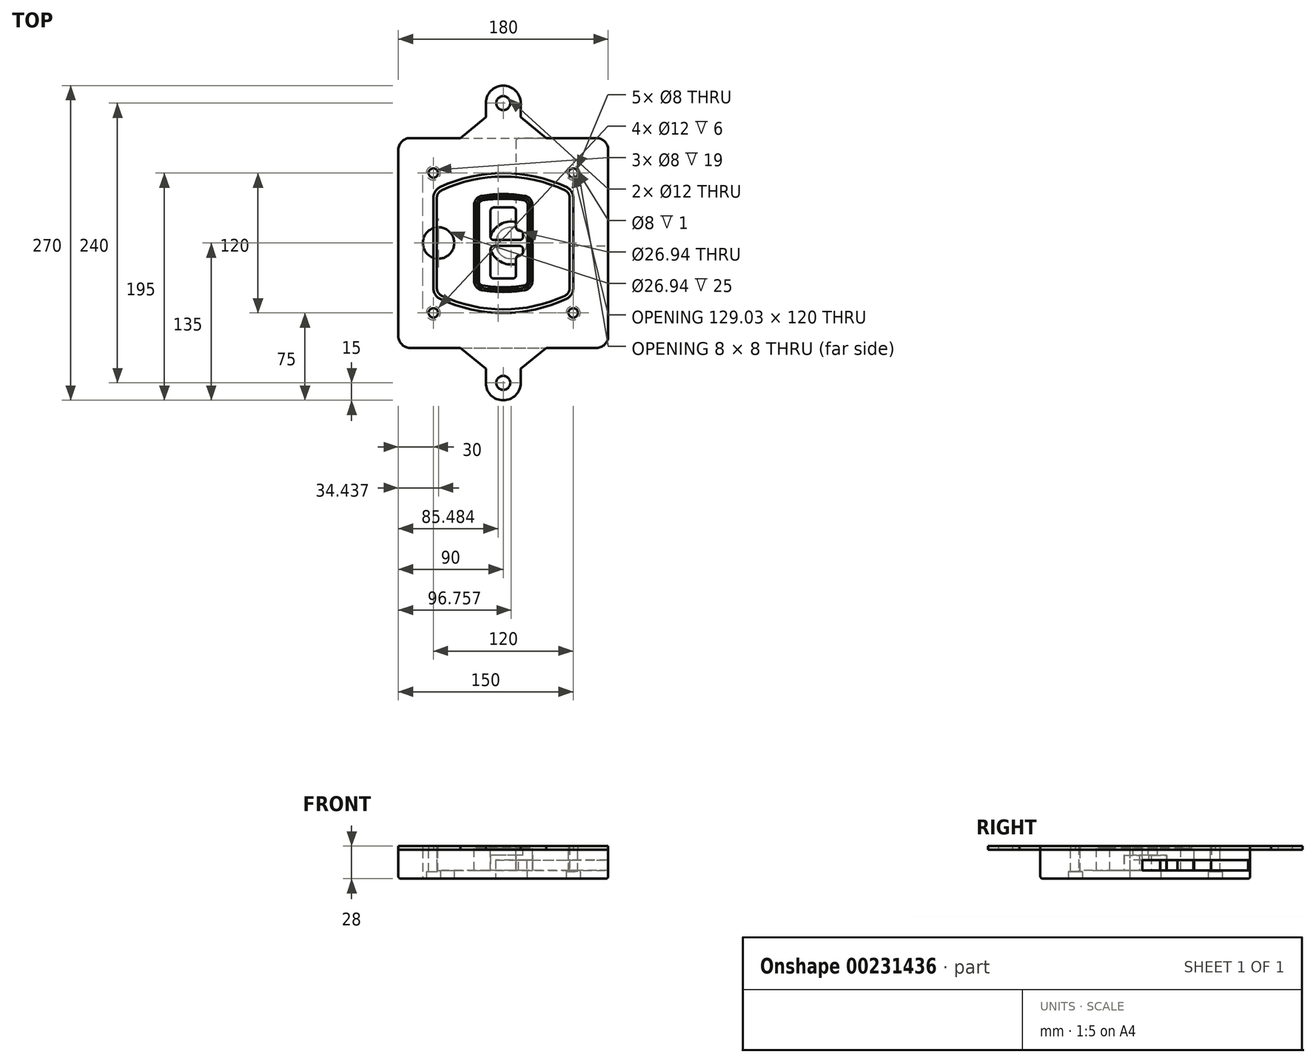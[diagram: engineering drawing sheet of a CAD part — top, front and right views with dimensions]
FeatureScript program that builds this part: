
annotation { "Feature Type Name" : "Feature", "Feature Type Description" : "" }
export const myFeature = defineFeature(function(context is Context, id is Id, definition is map)
    precondition{}
    {
        {
            var Q0;
            Q0=qCreatedBy(makeId("Top.planeOp"),FACE);
            var sketch = newSketch(context, id + "F0", { "sketchPlane" : qUnion([Q0])});
            skPoint(sketch, "E0.rect.middle", {"position": v(0, 0) * mm});
            skLineSegment(sketch, "E1.bottom", {"start": v(-80, -90) * mm, "end": v(80, -90) * mm});
            skLineSegment(sketch, "E1.top", {"start": v(-80, 90) * mm, "end": v(80, 90) * mm});
            skLineSegment(sketch, "E1.left", {"start": v(-90, -80) * mm, "end": v(-90, 80) * mm});
            skLineSegment(sketch, "E1.right", {"start": v(90, -80) * mm, "end": v(90, 80) * mm});
            skLineSegment(sketch, "E2", {"start": v(-90, 90) * mm, "end": v(90, -90) * mm, "construction": true});
            skLineSegment(sketch, "E3", {"start": v(90, 90) * mm, "end": v(-90, -90) * mm, "construction": true});
            skCircle(sketch, "E4", {"center": v(-60, 60) * mm, "radius": 4 * mm});
            skCircle(sketch, "E5", {"center": v(60, 60) * mm, "radius": 4 * mm});
            skCircle(sketch, "E6", {"center": v(60, -60) * mm, "radius": 4 * mm});
            skCircle(sketch, "E7", {"center": v(-60, -60) * mm, "radius": 4 * mm});
            skLineSegment(sketch, "E8", {"start": v(-60, 60) * mm, "end": v(60, 60) * mm, "construction": true});
            skLineSegment(sketch, "E9", {"start": v(60, 60) * mm, "end": v(60, -60) * mm, "construction": true});
            skLineSegment(sketch, "E10", {"start": v(60, -60) * mm, "end": v(-60, -60) * mm, "construction": true});
            skLineSegment(sketch, "E11", {"start": v(-60, -60) * mm, "end": v(-60, 60) * mm, "construction": true});
            skLineSegment(sketch, "E12", {"start": v(-60, 38.83) * mm, "end": v(-60, -38.83) * mm});
            skLineSegment(sketch, "E13", {"start": v(60, 38.83) * mm, "end": v(60, -38.83) * mm});
            skArc(sketch, "E14", {"start": v(54.26, 47.88) * mm, "mid": v(0, 60) * mm, "end": v(-54.26, 47.88) * mm});
            skArc(sketch, "E15", {"start": v(-54.26, -47.88) * mm, "mid": v(0, -60) * mm, "end": v(54.26, -47.88) * mm});
            skLineSegment(sketch, "E16", {"start": v(-60, 0) * mm, "end": v(60, 0) * mm, "construction": true});
            skPoint(sketch, "E17.visualSharp", {"position": v(-60, -45) * mm});
            skArc(sketch, "E17.filletArc", {"start": v(-60, -38.83) * mm, "mid": v(-58.44, -44.2) * mm, "end": v(-54.26, -47.88) * mm});
            skPoint(sketch, "E18.visualSharp", {"position": v(-60, 45) * mm});
            skArc(sketch, "E18.filletArc", {"start": v(-54.26, 47.88) * mm, "mid": v(-58.44, 44.2) * mm, "end": v(-60, 38.83) * mm});
            skPoint(sketch, "E19.visualSharp", {"position": v(60, 45) * mm});
            skArc(sketch, "E19.filletArc", {"start": v(60, 38.83) * mm, "mid": v(58.44, 44.2) * mm, "end": v(54.26, 47.88) * mm});
            skPoint(sketch, "E20.visualSharp", {"position": v(60, -45) * mm});
            skArc(sketch, "E20.filletArc", {"start": v(54.26, -47.88) * mm, "mid": v(58.44, -44.2) * mm, "end": v(60, -38.83) * mm});
            skPoint(sketch, "E21.visualSharp", {"position": v(-90, 90) * mm});
            skArc(sketch, "E21.filletArc", {"start": v(-80, 90) * mm, "mid": v(-87.07, 87.07) * mm, "end": v(-90, 80) * mm});
            skPoint(sketch, "E22.visualSharp", {"position": v(90, 90) * mm});
            skArc(sketch, "E22.filletArc", {"start": v(90, 80) * mm, "mid": v(87.07, 87.07) * mm, "end": v(80, 90) * mm});
            skPoint(sketch, "E23.visualSharp", {"position": v(90, -90) * mm});
            skArc(sketch, "E23.filletArc", {"start": v(80, -90) * mm, "mid": v(87.07, -87.07) * mm, "end": v(90, -80) * mm});
            skPoint(sketch, "E24.visualSharp", {"position": v(-90, -90) * mm});
            skArc(sketch, "E24.filletArc", {"start": v(-90, -80) * mm, "mid": v(-87.07, -87.07) * mm, "end": v(-80, -90) * mm});
            skArc(sketch, "E25.0", {"start": v(57, 38.83) * mm, "mid": v(55.9, 42.58) * mm, "end": v(52.98, 45.17) * mm});
            skLineSegment(sketch, "E25.1", {"start": v(57, 38.83) * mm, "end": v(57, -38.83) * mm});
            skArc(sketch, "E25.2", {"start": v(52.98, -45.17) * mm, "mid": v(55.9, -42.58) * mm, "end": v(57, -38.83) * mm});
            skArc(sketch, "E25.3", {"start": v(-52.98, -45.17) * mm, "mid": v(0, -57) * mm, "end": v(52.98, -45.17) * mm});
            skArc(sketch, "E25.4", {"start": v(-57, -38.83) * mm, "mid": v(-55.9, -42.58) * mm, "end": v(-52.98, -45.17) * mm});
            skArc(sketch, "E25.5", {"start": v(52.98, 45.17) * mm, "mid": v(0, 57) * mm, "end": v(-52.98, 45.17) * mm});
            skLineSegment(sketch, "E25.6", {"start": v(-57, 38.83) * mm, "end": v(-57, -38.83) * mm});
            skArc(sketch, "E25.7", {"start": v(-52.98, 45.17) * mm, "mid": v(-55.9, 42.58) * mm, "end": v(-57, 38.83) * mm});
            skArc(sketch, "E26.0", {"start": v(-55.96, 51.5) * mm, "mid": v(-61.82, 46.33) * mm, "end": v(-64, 38.83) * mm});
            skArc(sketch, "E26.1", {"start": v(55.96, 51.5) * mm, "mid": v(0, 64) * mm, "end": v(-55.96, 51.5) * mm});
            skArc(sketch, "E26.2", {"start": v(64, 38.83) * mm, "mid": v(61.82, 46.33) * mm, "end": v(55.96, 51.5) * mm});
            skLineSegment(sketch, "E26.3", {"start": v(64, 38.83) * mm, "end": v(64, -38.83) * mm});
            skArc(sketch, "E26.4", {"start": v(55.96, -51.5) * mm, "mid": v(61.82, -46.33) * mm, "end": v(64, -38.83) * mm});
            skLineSegment(sketch, "E26.5", {"start": v(-64, 38.83) * mm, "end": v(-64, -38.83) * mm});
            skArc(sketch, "E26.6", {"start": v(-55.96, -51.5) * mm, "mid": v(0, -64) * mm, "end": v(55.96, -51.5) * mm});
            skArc(sketch, "E26.7", {"start": v(-64, -38.83) * mm, "mid": v(-61.82, -46.33) * mm, "end": v(-55.96, -51.5) * mm});
            skSolve(sketch);
        }
        {
            var Q0;
            Q0=makeQuery(id+"F0.imprint","IMPRINT",FACE,{"disambiguationData":[TD([[makeQuery(id+"F0.imprint","IMPRINT",EDGE,{"derivedFrom":sQuery(id+"F0.wireOp",EDGE,"E1.bottom")}),1.0]])]});
            var Q1;
            Q1=makeQuery(id+"F0.imprint","IMPRINT",FACE,{"disambiguationData":[TD([[makeQuery(id+"F0.imprint","IMPRINT",EDGE,{"derivedFrom":sQuery(id+"F0.wireOp",EDGE,"E12")}),1.0]])]});
            var Q2;
            Q2=makeQuery(id+"F0.imprint","IMPRINT",FACE,{"disambiguationData":[TD([[makeQuery(id+"F0.imprint","IMPRINT",EDGE,{"derivedFrom":sQuery(id+"F0.wireOp",EDGE,"E25.0")}),1.0]])]});
            var Q3;
            Q3=makeQuery(id+"F0.imprint","IMPRINT",FACE,{"disambiguationData":[TD([[makeQuery(id+"F0.imprint","IMPRINT",EDGE,{"derivedFrom":sQuery(id+"F0.wireOp",EDGE,"E12")}),-1.0]])]});
            extrude(context, id + "F1", {"entities" : qUnion([Q0, Q1, Q2, Q3]), "oppositeDirection" : true, "depth" : 25 * mm});
        }
        {
            var Q0;
            Q0=makeQuery(id+"F0.imprint","IMPRINT",FACE,{"disambiguationData":[TD([[makeQuery(id+"F0.imprint","IMPRINT",EDGE,{"derivedFrom":sQuery(id+"F0.wireOp",EDGE,"E12")}),1.0]])]});
            extrude(context, id + "F2", {"entities" : qUnion([Q0]), "operationType" : NewBodyOperationType.ADD, "depth" : 3 * mm});
        }
        {
            var Q0;
            Q0=makeQuery(id+"F0.imprint","IMPRINT",FACE,{"disambiguationData":[TD([[makeQuery(id+"F0.imprint","IMPRINT",EDGE,{"derivedFrom":sQuery(id+"F0.wireOp",EDGE,"E25.0")}),1.0]])]});
            extrude(context, id + "F3", {"entities" : qUnion([Q0]), "operationType" : NewBodyOperationType.REMOVE, "oppositeDirection" : true, "depth" : 18 * mm});
        }
        {
            var Q0;
            Q0=makeQuery(id+"F2.opExtrude","CAP_FACE",FACE,{"disambiguationData":[OSD([sQuery(id+"F0.wireOp",EDGE,"E12"),sQuery(id+"F0.wireOp",EDGE,"E13"),sQuery(id+"F0.wireOp",EDGE,"E14"),sQuery(id+"F0.wireOp",EDGE,"E15"),sQuery(id+"F0.wireOp",EDGE,"E17.filletArc"),sQuery(id+"F0.wireOp",EDGE,"E18.filletArc"),sQuery(id+"F0.wireOp",EDGE,"E19.filletArc"),sQuery(id+"F0.wireOp",EDGE,"E20.filletArc"),sQuery(id+"F0.wireOp",EDGE,"E25.0"),sQuery(id+"F0.wireOp",EDGE,"E25.1"),sQuery(id+"F0.wireOp",EDGE,"E25.2"),sQuery(id+"F0.wireOp",EDGE,"E25.3"),sQuery(id+"F0.wireOp",EDGE,"E25.4"),sQuery(id+"F0.wireOp",EDGE,"E25.5"),sQuery(id+"F0.wireOp",EDGE,"E25.6"),sQuery(id+"F0.wireOp",EDGE,"E25.7")])],"isStart":false});
            var sketch = newSketch(context, id + "F4", { "sketchPlane" : qUnion([Q0])});
            skArc(sketch, "E27.0", {"start": v(-18.34, -40.45) * mm, "mid": v(0, -42) * mm, "end": v(18.34, -40.45) * mm});
            skArc(sketch, "E28.0", {"start": v(18.34, 40.45) * mm, "mid": v(0, 42) * mm, "end": v(-18.34, 40.45) * mm});
            skLineSegment(sketch, "E29", {"start": v(-25, 32.57) * mm, "end": v(-25, -32.57) * mm});
            skLineSegment(sketch, "E30", {"start": v(25, 32.57) * mm, "end": v(25, -32.57) * mm});
            skLineSegment(sketch, "E31", {"start": v(-25, 39.1) * mm, "end": v(25, 39.1) * mm, "construction": true});
            skLineSegment(sketch, "E32", {"start": v(-25, -39.1) * mm, "end": v(25, -39.1) * mm, "construction": true});
            skPoint(sketch, "E33.visualSharp", {"position": v(-25, 39.1) * mm});
            skArc(sketch, "E33.filletArc", {"start": v(-18.34, 40.45) * mm, "mid": v(-23.11, 37.73) * mm, "end": v(-25, 32.57) * mm});
            skPoint(sketch, "E34.visualSharp", {"position": v(25, 39.1) * mm});
            skArc(sketch, "E34.filletArc", {"start": v(25, 32.57) * mm, "mid": v(23.11, 37.73) * mm, "end": v(18.34, 40.45) * mm});
            skPoint(sketch, "E35.visualSharp", {"position": v(25, -39.1) * mm});
            skArc(sketch, "E35.filletArc", {"start": v(18.34, -40.45) * mm, "mid": v(23.11, -37.73) * mm, "end": v(25, -32.57) * mm});
            skPoint(sketch, "E36.visualSharp", {"position": v(-25, -39.1) * mm});
            skArc(sketch, "E36.filletArc", {"start": v(-25, -32.57) * mm, "mid": v(-23.11, -37.73) * mm, "end": v(-18.34, -40.45) * mm});
            skArc(sketch, "E37.0", {"start": v(52.98, 45.17) * mm, "mid": v(0, 57) * mm, "end": v(-52.98, 45.17) * mm});
            skArc(sketch, "E37.1", {"start": v(-52.98, 45.17) * mm, "mid": v(-55.9, 42.58) * mm, "end": v(-57, 38.83) * mm});
            skLineSegment(sketch, "E37.2", {"start": v(-57, 38.83) * mm, "end": v(-57, -38.83) * mm});
            skArc(sketch, "E37.3", {"start": v(-57, -38.83) * mm, "mid": v(-55.9, -42.58) * mm, "end": v(-52.98, -45.17) * mm});
            skArc(sketch, "E37.4", {"start": v(-52.98, -45.17) * mm, "mid": v(0, -57) * mm, "end": v(52.98, -45.17) * mm});
            skArc(sketch, "E37.5", {"start": v(52.98, -45.17) * mm, "mid": v(55.9, -42.58) * mm, "end": v(57, -38.83) * mm});
            skLineSegment(sketch, "E37.6", {"start": v(57, 38.83) * mm, "end": v(57, -38.83) * mm});
            skArc(sketch, "E37.7", {"start": v(57, 38.83) * mm, "mid": v(55.9, 42.58) * mm, "end": v(52.98, 45.17) * mm});
            skLineSegment(sketch, "E38.0", {"start": v(23, 32.57) * mm, "end": v(23, -32.57) * mm});
            skArc(sketch, "E38.1", {"start": v(18, -38.48) * mm, "mid": v(21.58, -36.44) * mm, "end": v(23, -32.57) * mm});
            skArc(sketch, "E38.2", {"start": v(-18, -38.48) * mm, "mid": v(0, -40) * mm, "end": v(18, -38.48) * mm});
            skArc(sketch, "E38.3", {"start": v(-23, -32.57) * mm, "mid": v(-21.58, -36.44) * mm, "end": v(-18, -38.48) * mm});
            skLineSegment(sketch, "E38.4", {"start": v(-23, 32.57) * mm, "end": v(-23, -32.57) * mm});
            skArc(sketch, "E38.5", {"start": v(23, 32.57) * mm, "mid": v(21.58, 36.44) * mm, "end": v(18, 38.48) * mm});
            skArc(sketch, "E38.6", {"start": v(-18, 38.48) * mm, "mid": v(-21.58, 36.44) * mm, "end": v(-23, 32.57) * mm});
            skArc(sketch, "E38.7", {"start": v(18, 38.48) * mm, "mid": v(0, 40) * mm, "end": v(-18, 38.48) * mm});
            skArc(sketch, "E39.0", {"start": v(21, 32.57) * mm, "mid": v(20.06, 35.15) * mm, "end": v(17.67, 36.5) * mm});
            skLineSegment(sketch, "E39.1", {"start": v(21, 32.57) * mm, "end": v(21, -32.57) * mm});
            skArc(sketch, "E39.2", {"start": v(17.67, -36.5) * mm, "mid": v(20.06, -35.15) * mm, "end": v(21, -32.57) * mm});
            skArc(sketch, "E39.3", {"start": v(-17.67, -36.5) * mm, "mid": v(0, -38) * mm, "end": v(17.67, -36.5) * mm});
            skArc(sketch, "E39.4", {"start": v(-21, -32.57) * mm, "mid": v(-20.06, -35.15) * mm, "end": v(-17.67, -36.5) * mm});
            skArc(sketch, "E39.5", {"start": v(17.67, 36.5) * mm, "mid": v(0, 38) * mm, "end": v(-17.67, 36.5) * mm});
            skLineSegment(sketch, "E39.6", {"start": v(-21, 32.57) * mm, "end": v(-21, -32.57) * mm});
            skArc(sketch, "E39.7", {"start": v(-17.67, 36.5) * mm, "mid": v(-20.06, 35.15) * mm, "end": v(-21, 32.57) * mm});
            skLineSegment(sketch, "E40", {"start": v(-25, 0) * mm, "end": v(25, 0) * mm, "construction": true});
            skLineSegment(sketch, "E41", {"start": v(-11, 5.5) * mm, "end": v(-11, 27.5) * mm});
            skLineSegment(sketch, "E42", {"start": v(-8, 30.5) * mm, "end": v(8, 30.5) * mm});
            skLineSegment(sketch, "E43", {"start": v(11, 27.5) * mm, "end": v(11, 13.5) * mm});
            skLineSegment(sketch, "E44", {"start": v(14, 10.5) * mm, "end": v(14, 10.5) * mm});
            skLineSegment(sketch, "E45", {"start": v(17, 7.5) * mm, "end": v(17, 5.5) * mm});
            skLineSegment(sketch, "E46", {"start": v(14, 2.5) * mm, "end": v(-8, 2.5) * mm});
            skPoint(sketch, "E47.visualSharp", {"position": v(-11, 30.5) * mm});
            skArc(sketch, "E47.filletArc", {"start": v(-8, 30.5) * mm, "mid": v(-10.12, 29.62) * mm, "end": v(-11, 27.5) * mm});
            skPoint(sketch, "E48.visualSharp", {"position": v(11, 30.5) * mm});
            skArc(sketch, "E48.filletArc", {"start": v(11, 27.5) * mm, "mid": v(10.12, 29.62) * mm, "end": v(8, 30.5) * mm});
            skPoint(sketch, "E49.visualSharp", {"position": v(11, 10.5) * mm});
            skArc(sketch, "E49.filletArc", {"start": v(11, 13.5) * mm, "mid": v(11.88, 11.38) * mm, "end": v(14, 10.5) * mm});
            skPoint(sketch, "E50.visualSharp", {"position": v(17, 10.5) * mm});
            skArc(sketch, "E50.filletArc", {"start": v(17, 7.5) * mm, "mid": v(16.12, 9.62) * mm, "end": v(14, 10.5) * mm});
            skPoint(sketch, "E51.visualSharp", {"position": v(17, 2.5) * mm});
            skArc(sketch, "E51.filletArc", {"start": v(14, 2.5) * mm, "mid": v(16.12, 3.38) * mm, "end": v(17, 5.5) * mm});
            skPoint(sketch, "E52.visualSharp", {"position": v(-11, 2.5) * mm});
            skArc(sketch, "E52.filletArc", {"start": v(-11, 5.5) * mm, "mid": v(-10.12, 3.38) * mm, "end": v(-8, 2.5) * mm});
            skLineSegment(sketch, "E53.0.MirrorCS", {"start": v(14, -2.5) * mm, "end": v(-8, -2.5) * mm});
            skArc(sketch, "E54.0.MirrorCS", {"start": v(-11, -5.5) * mm, "mid": v(-10.12, -3.38) * mm, "end": v(-8, -2.5) * mm});
            skLineSegment(sketch, "E55.0.MirrorCS", {"start": v(-11, -5.5) * mm, "end": v(-11, -27.5) * mm});
            skArc(sketch, "E56.0.MirrorCS", {"start": v(-8, -30.5) * mm, "mid": v(-10.12, -29.62) * mm, "end": v(-11, -27.5) * mm});
            skLineSegment(sketch, "E57.0.MirrorCS", {"start": v(-8, -30.5) * mm, "end": v(8, -30.5) * mm});
            skArc(sketch, "E58.0.MirrorCS", {"start": v(11, -27.5) * mm, "mid": v(10.12, -29.62) * mm, "end": v(8, -30.5) * mm});
            skLineSegment(sketch, "E59.0.MirrorCS", {"start": v(11, -27.5) * mm, "end": v(11, -13.5) * mm});
            skArc(sketch, "E60.0.MirrorCS", {"start": v(11, -13.5) * mm, "mid": v(11.88, -11.38) * mm, "end": v(14, -10.5) * mm});
            skArc(sketch, "E61.0.MirrorCS", {"start": v(17, -7.5) * mm, "mid": v(16.12, -9.62) * mm, "end": v(14, -10.5) * mm});
            skLineSegment(sketch, "E62.0.MirrorCS", {"start": v(17, -7.5) * mm, "end": v(17, -5.5) * mm});
            skArc(sketch, "E63.0.MirrorCS", {"start": v(14, -2.5) * mm, "mid": v(16.12, -3.38) * mm, "end": v(17, -5.5) * mm});
            skSolve(sketch);
        }
        {
            var Q0;
            Q0=makeQuery(id+"F4.imprint","IMPRINT",FACE,{"disambiguationData":[TD([[makeQuery(id+"F4.imprint","IMPRINT",EDGE,{"derivedFrom":sQuery(id+"F4.wireOp",EDGE,"E27.0")}),1.0]])]});
            var Q1;
            Q1=makeQuery(id+"F4.imprint","IMPRINT",FACE,{"disambiguationData":[TD([[makeQuery(id+"F4.imprint","IMPRINT",EDGE,{"derivedFrom":sQuery(id+"F4.wireOp",EDGE,"E38.0")}),-1.0]])]});
            var Q2;
            Q2=makeQuery(id+"F4.imprint","IMPRINT",FACE,{"disambiguationData":[TD([[makeQuery(id+"F4.imprint","IMPRINT",EDGE,{"derivedFrom":sQuery(id+"F4.wireOp",EDGE,"E39.0")}),1.0]])]});
            extrude(context, id + "F5", {"entities" : qUnion([Q0, Q1, Q2]), "operationType" : NewBodyOperationType.ADD, "endBound" : BoundingType.UP_TO_NEXT, "oppositeDirection" : true, "depth" : 25 * mm});
        }
        {
            var Q0;
            Q0=makeQuery(id+"F4.imprint","IMPRINT",FACE,{"disambiguationData":[TD([[makeQuery(id+"F4.imprint","IMPRINT",EDGE,{"derivedFrom":sQuery(id+"F4.wireOp",EDGE,"E38.0")}),-1.0]])]});
            extrude(context, id + "F6", {"entities" : qUnion([Q0]), "operationType" : NewBodyOperationType.REMOVE, "oppositeDirection" : true, "depth" : 2 * mm});
        }
        {
            var Q0;
            Q0=makeQuery(id+"F1.opExtrude","CAP_FACE",FACE,{"disambiguationData":[OSD([sQuery(id+"F0.wireOp",EDGE,"E1.bottom"),sQuery(id+"F0.wireOp",EDGE,"E1.top"),sQuery(id+"F0.wireOp",EDGE,"E1.left"),sQuery(id+"F0.wireOp",EDGE,"E1.right"),sQuery(id+"F0.wireOp",EDGE,"E4"),sQuery(id+"F0.wireOp",EDGE,"E5"),sQuery(id+"F0.wireOp",EDGE,"E6"),sQuery(id+"F0.wireOp",EDGE,"E7"),sQuery(id+"F0.wireOp",EDGE,"E21.filletArc"),sQuery(id+"F0.wireOp",EDGE,"E22.filletArc"),sQuery(id+"F0.wireOp",EDGE,"E23.filletArc"),sQuery(id+"F0.wireOp",EDGE,"E24.filletArc")])],"isStart":false});
            var sketch = newSketch(context, id + "F7", { "sketchPlane" : qUnion([Q0])});
            skCircle(sketch, "E64", {"center": v(6.76, 0) * mm, "radius": 13.47 * mm});
            skCircle(sketch, "E65", {"center": v(-55.56, 0) * mm, "radius": 13.47 * mm});
            skLineSegment(sketch, "E66", {"start": v(90, 0) * mm, "end": v(-90, 0) * mm});
            skCircle(sketch, "E67", {"center": v(6.76, 0) * mm, "radius": 18.47 * mm});
            skCircle(sketch, "E68", {"center": v(60, -60) * mm, "radius": 6 * mm});
            skCircle(sketch, "E69", {"center": v(-60, -60) * mm, "radius": 6 * mm});
            skCircle(sketch, "E70", {"center": v(-60, 60) * mm, "radius": 6 * mm});
            skCircle(sketch, "E71", {"center": v(60, 60) * mm, "radius": 6 * mm});
            skSolve(sketch);
        }
        {
            var Q0;
            {var subQ1=sQuery(id+"F7.wireOp",EDGE,"E66");var subQ4=sQuery(id+"F7.wireOp",EDGE,"E64");var subQ6=makeQuery(id+"F7.imprint","INTERSECT",VERTEX,{"disambiguationData":[OD(0.0)],"derivedFrom":[subQ4,subQ1]});Q0=makeQuery(id+"F7.imprint","IMPRINT",FACE,{"disambiguationData":[TD([[makeQuery(id+"F7.imprint","IMPRINT",EDGE,{"disambiguationData":[TD([[subQ6,-1.0]])],"derivedFrom":subQ4}),-1.0]])]});}
            var Q1;
            {var subQ0=sQuery(id+"F7.wireOp",EDGE,"E66");var subQ1=sQuery(id+"F7.wireOp",EDGE,"E64");var subQ3=makeQuery(id+"F7.imprint","INTERSECT",VERTEX,{"disambiguationData":[OD(0.0)],"derivedFrom":[subQ1,subQ0]});Q1=makeQuery(id+"F7.imprint","IMPRINT",FACE,{"disambiguationData":[TD([[makeQuery(id+"F7.imprint","IMPRINT",EDGE,{"disambiguationData":[TD([[subQ3,-1.0]])],"derivedFrom":subQ1}),1.0]])]});}
            var Q2;
            {var subQ0=sQuery(id+"F7.wireOp",EDGE,"E66");var subQ1=sQuery(id+"F7.wireOp",EDGE,"E64");var subQ3=makeQuery(id+"F7.imprint","INTERSECT",VERTEX,{"disambiguationData":[OD(0.0)],"derivedFrom":[subQ1,subQ0]});Q2=makeQuery(id+"F7.imprint","IMPRINT",FACE,{"disambiguationData":[TD([[makeQuery(id+"F7.imprint","IMPRINT",EDGE,{"disambiguationData":[TD([[subQ3,1.0]])],"derivedFrom":subQ1}),1.0]])]});}
            var Q3;
            {var subQ1=sQuery(id+"F7.wireOp",EDGE,"E66");var subQ4=sQuery(id+"F7.wireOp",EDGE,"E64");var subQ6=makeQuery(id+"F7.imprint","INTERSECT",VERTEX,{"disambiguationData":[OD(0.0)],"derivedFrom":[subQ4,subQ1]});Q3=makeQuery(id+"F7.imprint","IMPRINT",FACE,{"disambiguationData":[TD([[makeQuery(id+"F7.imprint","IMPRINT",EDGE,{"disambiguationData":[TD([[subQ6,1.0]])],"derivedFrom":subQ4}),-1.0]])]});}
            extrude(context, id + "F8", {"entities" : qUnion([Q0, Q1, Q2, Q3]), "operationType" : NewBodyOperationType.ADD, "oppositeDirection" : true, "depth" : 20 * mm});
        }
        {
            var Q0;
            {var subQ0=sQuery(id+"F7.wireOp",EDGE,"E66");var subQ1=sQuery(id+"F7.wireOp",EDGE,"E64");var subQ3=makeQuery(id+"F7.imprint","INTERSECT",VERTEX,{"disambiguationData":[OD(0.0)],"derivedFrom":[subQ1,subQ0]});Q0=makeQuery(id+"F7.imprint","IMPRINT",FACE,{"disambiguationData":[TD([[makeQuery(id+"F7.imprint","IMPRINT",EDGE,{"disambiguationData":[TD([[subQ3,-1.0]])],"derivedFrom":subQ1}),1.0]])]});}
            var Q1;
            {var subQ0=sQuery(id+"F7.wireOp",EDGE,"E66");var subQ1=sQuery(id+"F7.wireOp",EDGE,"E64");var subQ3=makeQuery(id+"F7.imprint","INTERSECT",VERTEX,{"disambiguationData":[OD(0.0)],"derivedFrom":[subQ1,subQ0]});Q1=makeQuery(id+"F7.imprint","IMPRINT",FACE,{"disambiguationData":[TD([[makeQuery(id+"F7.imprint","IMPRINT",EDGE,{"disambiguationData":[TD([[subQ3,1.0]])],"derivedFrom":subQ1}),1.0]])]});}
            extrude(context, id + "F9", {"entities" : qUnion([Q0, Q1]), "operationType" : NewBodyOperationType.REMOVE, "oppositeDirection" : true, "depth" : 16 * mm});
        }
        {
            var Q0;
            {var subQ0=sQuery(id+"F7.wireOp",EDGE,"E66");var subQ1=sQuery(id+"F7.wireOp",EDGE,"E65");var subQ3=makeQuery(id+"F7.imprint","INTERSECT",VERTEX,{"disambiguationData":[OD(0.0)],"derivedFrom":[subQ1,subQ0]});Q0=makeQuery(id+"F7.imprint","IMPRINT",FACE,{"disambiguationData":[TD([[makeQuery(id+"F7.imprint","IMPRINT",EDGE,{"disambiguationData":[TD([[subQ3,-1.0]])],"derivedFrom":subQ1}),1.0]])]});}
            var Q1;
            {var subQ0=sQuery(id+"F7.wireOp",EDGE,"E66");var subQ1=sQuery(id+"F7.wireOp",EDGE,"E65");var subQ3=makeQuery(id+"F7.imprint","INTERSECT",VERTEX,{"disambiguationData":[OD(0.0)],"derivedFrom":[subQ1,subQ0]});Q1=makeQuery(id+"F7.imprint","IMPRINT",FACE,{"disambiguationData":[TD([[makeQuery(id+"F7.imprint","IMPRINT",EDGE,{"disambiguationData":[TD([[subQ3,1.0]])],"derivedFrom":subQ1}),1.0]])]});}
            extrude(context, id + "F10", {"entities" : qUnion([Q0, Q1]), "operationType" : NewBodyOperationType.REMOVE, "oppositeDirection" : true, "depth" : 25 * mm});
        }
        {
            var Q0;
            Q0=makeQuery(id+"F7.imprint","IMPRINT",FACE,{"disambiguationData":[TD([[makeQuery(id+"F7.imprint","IMPRINT",EDGE,{"derivedFrom":sQuery(id+"F7.wireOp",EDGE,"E68")}),1.0]])]});
            var Q1;
            Q1=makeQuery(id+"F7.imprint","IMPRINT",FACE,{"disambiguationData":[TD([[makeQuery(id+"F7.imprint","IMPRINT",EDGE,{"derivedFrom":makeQuery(id+"F1.opExtrude","CAP_EDGE",EDGE,{"disambiguationData":[OSD([sQuery(id+"F0.wireOp",EDGE,"E5")])],"isStart":false})}),-1.0]])]});
            var Q2;
            Q2=makeQuery(id+"F7.imprint","IMPRINT",FACE,{"disambiguationData":[TD([[makeQuery(id+"F7.imprint","IMPRINT",EDGE,{"derivedFrom":sQuery(id+"F7.wireOp",EDGE,"E69")}),1.0]])]});
            var Q3;
            Q3=makeQuery(id+"F7.imprint","IMPRINT",FACE,{"disambiguationData":[TD([[makeQuery(id+"F7.imprint","IMPRINT",EDGE,{"derivedFrom":makeQuery(id+"F1.opExtrude","CAP_EDGE",EDGE,{"disambiguationData":[OSD([sQuery(id+"F0.wireOp",EDGE,"E4")])],"isStart":false})}),-1.0]])]});
            var Q4;
            Q4=makeQuery(id+"F7.imprint","IMPRINT",FACE,{"disambiguationData":[TD([[makeQuery(id+"F7.imprint","IMPRINT",EDGE,{"derivedFrom":sQuery(id+"F7.wireOp",EDGE,"E70")}),1.0]])]});
            var Q5;
            Q5=makeQuery(id+"F7.imprint","IMPRINT",FACE,{"disambiguationData":[TD([[makeQuery(id+"F7.imprint","IMPRINT",EDGE,{"derivedFrom":makeQuery(id+"F1.opExtrude","CAP_EDGE",EDGE,{"disambiguationData":[OSD([sQuery(id+"F0.wireOp",EDGE,"E7")])],"isStart":false})}),-1.0]])]});
            var Q6;
            Q6=makeQuery(id+"F7.imprint","IMPRINT",FACE,{"disambiguationData":[TD([[makeQuery(id+"F7.imprint","IMPRINT",EDGE,{"derivedFrom":sQuery(id+"F7.wireOp",EDGE,"E71")}),1.0]])]});
            var Q7;
            Q7=makeQuery(id+"F7.imprint","IMPRINT",FACE,{"disambiguationData":[TD([[makeQuery(id+"F7.imprint","IMPRINT",EDGE,{"derivedFrom":makeQuery(id+"F1.opExtrude","CAP_EDGE",EDGE,{"disambiguationData":[OSD([sQuery(id+"F0.wireOp",EDGE,"E6")])],"isStart":false})}),-1.0]])]});
            extrude(context, id + "F11", {"entities" : qUnion([Q0, Q1, Q2, Q3, Q4, Q5, Q6, Q7]), "operationType" : NewBodyOperationType.REMOVE, "oppositeDirection" : true, "depth" : 6 * mm});
        }
        {
            var Q0;
            Q0=makeQuery(id+"F9.boolean.opBoolean","COPY",FACE,{"derivedFrom":makeQuery(id+"F9.opExtrude","CAP_FACE",FACE,{"disambiguationData":[OSD([sQuery(id+"F7.wireOp",EDGE,"E64")])],"isStart":false})});
            var sketch = newSketch(context, id + "F12", { "sketchPlane" : qUnion([Q0])});
            skArc(sketch, "E72.0", {"start": v(11, -88.19) * mm, "mid": v(97.1, -83.6) * mm, "end": v(92.5, 2.5) * mm});
            skLineSegment(sketch, "E72.1", {"start": v(11, -17.97) * mm, "end": v(11, -17.97) * mm});
            skLineSegment(sketch, "E73", {"start": v(92.5, -105.13) * mm, "end": v(102.3, -105.13) * mm});
            skLineSegment(sketch, "E74.0", {"start": v(92.5, 2.5) * mm, "end": v(14, 2.5) * mm});
            skArc(sketch, "E74.1", {"start": v(14, 2.5) * mm, "mid": v(16.12, 3.38) * mm, "end": v(17, 5.5) * mm});
            skLineSegment(sketch, "E74.2", {"start": v(17, 7.5) * mm, "end": v(17, 5.5) * mm});
            skArc(sketch, "E74.3", {"start": v(17, 7.5) * mm, "mid": v(16.12, 9.62) * mm, "end": v(14, 10.5) * mm});
            skArc(sketch, "E74.4", {"start": v(11, 13.5) * mm, "mid": v(11.88, 11.38) * mm, "end": v(14, 10.5) * mm});
            skLineSegment(sketch, "E74.5", {"start": v(11, 13.5) * mm, "end": v(11, -88.19) * mm});
            skLineSegment(sketch, "E74.7", {"start": v(92.5, -2.5) * mm, "end": v(14, -2.5) * mm});
            skArc(sketch, "E74.8", {"start": v(14, -2.5) * mm, "mid": v(16.12, -3.38) * mm, "end": v(17, -5.5) * mm});
            skLineSegment(sketch, "E74.9", {"start": v(17, -7.5) * mm, "end": v(17, -5.5) * mm});
            skArc(sketch, "E74.10", {"start": v(17, -7.5) * mm, "mid": v(16.12, -9.62) * mm, "end": v(14, -10.5) * mm});
            skArc(sketch, "E74.11", {"start": v(11, -13.5) * mm, "mid": v(11.88, -11.38) * mm, "end": v(14, -10.5) * mm});
            skLineSegment(sketch, "E74.12", {"start": v(11, -17.97) * mm, "end": v(11, -13.5) * mm});
            skPoint(sketch, "E75.orphan", {"position": v(11, -27.5) * mm});
            skPoint(sketch, "E76.orphan", {"position": v(-8, -2.5) * mm});
            skPoint(sketch, "E77.orphan", {"position": v(-8, 2.5) * mm});
            skPoint(sketch, "E78.orphan", {"position": v(11, 27.5) * mm});
            skSolve(sketch);
        }
        {
            var Q0;
            {var subQ7=sQuery(id+"F12.wireOp",EDGE,"E72.0");var subQ14=sQuery(id+"F12.wireOp",EDGE,"E72.1");var subQ16=sQuery(id+"F12.wireOp",EDGE,"E74.1");var subQ18=sQuery(id+"F12.wireOp",EDGE,"E74.8");Q0=qUnion([makeQuery(id+"F12.imprint","IMPRINT",FACE,{"disambiguationData":[TD([[makeQuery(id+"F12.imprint","IMPRINT",EDGE,{"derivedFrom":subQ7}),1.0]])]}),makeQuery(id+"F12.imprint","IMPRINT",FACE,{"disambiguationData":[TD([[makeQuery(id+"F12.imprint","IMPRINT",EDGE,{"derivedFrom":subQ14}),1.0]])]}),makeQuery(id+"F12.imprint","IMPRINT",FACE,{"disambiguationData":[TD([[makeQuery(id+"F12.imprint","IMPRINT",EDGE,{"derivedFrom":subQ16}),1.0]])]}),makeQuery(id+"F12.imprint","IMPRINT",FACE,{"disambiguationData":[TD([[makeQuery(id+"F12.imprint","IMPRINT",EDGE,{"derivedFrom":subQ18}),-1.0]])]})]);}
            var Q1;
            Q1=makeQuery(id+"F5.boolean.opBoolean","SPLIT",FACE,{"disambiguationData":[TD([makeQuery(id+"F5.opExtrude","SWEPT_FACE",FACE,{"disambiguationData":[OSD([sQuery(id+"F4.wireOp",EDGE,"E41")])]})])],"derivedFrom":makeQuery(id+"F3.boolean.opBoolean","COPY",FACE,{"derivedFrom":makeQuery(id+"F3.opExtrude","CAP_FACE",FACE,{"disambiguationData":[OSD([sQuery(id+"F0.wireOp",EDGE,"E25.0"),sQuery(id+"F0.wireOp",EDGE,"E25.1"),sQuery(id+"F0.wireOp",EDGE,"E25.2"),sQuery(id+"F0.wireOp",EDGE,"E25.3"),sQuery(id+"F0.wireOp",EDGE,"E25.4"),sQuery(id+"F0.wireOp",EDGE,"E25.5"),sQuery(id+"F0.wireOp",EDGE,"E25.6"),sQuery(id+"F0.wireOp",EDGE,"E25.7")])],"isStart":false})})});
            extrude(context, id + "F13", {"entities" : qUnion([Q0]), "operationType" : NewBodyOperationType.REMOVE, "endBound" : BoundingType.UP_TO_SURFACE, "endBoundEntityFace" : qUnion([Q1]), "depth" : 25 * mm});
        }
        {
            var Q0;
            Q0=makeQuery(id+"F1.opExtrude","CAP_EDGE",EDGE,{"disambiguationData":[OSD([sQuery(id+"F0.wireOp",EDGE,"E1.bottom")])],"isStart":false});
            fillet(context, id + "F14", {"entities" : qUnion([Q0]), "radius" : 2 * mm, "tangentPropagation" : true, "allowEdgeOverflow" : false});
        }
        {
            var Q0;
            {var subQ0=sQuery(id+"F0.wireOp",EDGE,"E22.filletArc");var subQ1=sQuery(id+"F0.wireOp",EDGE,"E7");var subQ2=sQuery(id+"F0.wireOp",EDGE,"E6");var subQ3=sQuery(id+"F0.wireOp",EDGE,"E5");var subQ4=sQuery(id+"F0.wireOp",EDGE,"E4");var subQ5=sQuery(id+"F0.wireOp",EDGE,"E1.bottom");var subQ6=sQuery(id+"F0.wireOp",EDGE,"E21.filletArc");var subQ7=sQuery(id+"F0.wireOp",EDGE,"E1.top");var subQ8=sQuery(id+"F0.wireOp",EDGE,"E1.left");var subQ9=sQuery(id+"F0.wireOp",EDGE,"E1.right");var subQ10=sQuery(id+"F0.wireOp",EDGE,"E23.filletArc");var subQ11=sQuery(id+"F0.wireOp",EDGE,"E24.filletArc");Q0=makeQuery(id+"F2.boolean.opBoolean","SPLIT",FACE,{"disambiguationData":[TD([makeQuery(id+"F1.opExtrude","SWEPT_FACE",FACE,{"disambiguationData":[OSD([subQ5])]})])],"derivedFrom":makeQuery(id+"F1.opExtrude","CAP_FACE",FACE,{"disambiguationData":[OSD([subQ5,subQ7,subQ8,subQ9,subQ4,subQ3,subQ2,subQ1,subQ6,subQ0,subQ10,subQ11])],"isStart":true})});}
            var sketch = newSketch(context, id + "F15", { "sketchPlane" : qUnion([Q0])});
            skLineSegment(sketch, "E79", {"start": v(0, 90) * mm, "end": v(0, 120) * mm});
            skCircle(sketch, "E80", {"center": v(0, 120) * mm, "radius": 6 * mm});
            skArc(sketch, "E81", {"start": v(15, 120) * mm, "mid": v(0, 135) * mm, "end": v(-15, 120) * mm});
            skLineSegment(sketch, "E82", {"start": v(15, 120) * mm, "end": v(15, 108) * mm});
            skLineSegment(sketch, "E83", {"start": v(-15, 120) * mm, "end": v(-15, 108) * mm});
            skLineSegment(sketch, "E84", {"start": v(-15, 108) * mm, "end": v(-36.82, 90) * mm});
            skLineSegment(sketch, "E85.MirrorCS", {"start": v(15, 108) * mm, "end": v(36.82, 90) * mm});
            skLineSegment(sketch, "E86.MirrorCS", {"start": v(-15, -120) * mm, "end": v(-15, -108) * mm});
            skLineSegment(sketch, "E87.MirrorCS", {"start": v(0, -90) * mm, "end": v(0, -120) * mm});
            skLineSegment(sketch, "E88.MirrorCS", {"start": v(15, -108) * mm, "end": v(36.82, -90) * mm});
            skArc(sketch, "E89.MirrorCS", {"start": v(15, -120) * mm, "mid": v(0, -135) * mm, "end": v(-15, -120) * mm});
            skCircle(sketch, "E90.MirrorC", {"center": v(0, -120) * mm, "radius": 6 * mm});
            skLineSegment(sketch, "E91.MirrorCS", {"start": v(15, -120) * mm, "end": v(15, -108) * mm});
            skLineSegment(sketch, "E92.MirrorCS", {"start": v(-15, -108) * mm, "end": v(-36.82, -90) * mm});
            skSolve(sketch);
        }
        {
            var Q0;
            Q0=makeQuery(id+"F15.imprint","IMPRINT",FACE,{"disambiguationData":[TD([[makeQuery(id+"F15.imprint","IMPRINT",EDGE,{"derivedFrom":makeQuery(id+"F1.opExtrude","CAP_EDGE",EDGE,{"disambiguationData":[OSD([sQuery(id+"F0.wireOp",EDGE,"E4")])],"isStart":true})}),-1.0]])]});
            var Q1;
            Q1=makeQuery(id+"F15.imprint","IMPRINT",FACE,{"disambiguationData":[TD([[makeQuery(id+"F15.imprint","IMPRINT",EDGE,{"derivedFrom":makeQuery(id+"F1.opExtrude","CAP_EDGE",EDGE,{"disambiguationData":[OSD([sQuery(id+"F0.wireOp",EDGE,"E6")])],"isStart":true})}),-1.0]])]});
            var Q2;
            Q2=makeQuery(id+"F15.imprint","IMPRINT",FACE,{"disambiguationData":[TD([[makeQuery(id+"F15.imprint","IMPRINT",EDGE,{"derivedFrom":sQuery(id+"F15.wireOp",EDGE,"E86.MirrorCS")}),-1.0]])]});
            var Q3;
            Q3=makeQuery(id+"F15.imprint","IMPRINT",FACE,{"disambiguationData":[TD([[makeQuery(id+"F15.imprint","IMPRINT",EDGE,{"derivedFrom":sQuery(id+"F15.wireOp",EDGE,"E80")}),-1.0]])]});
            var Q4;
            Q4=makeQuery(id+"F2.opExtrude","CAP_FACE",FACE,{"disambiguationData":[OSD([sQuery(id+"F0.wireOp",EDGE,"E12"),sQuery(id+"F0.wireOp",EDGE,"E13"),sQuery(id+"F0.wireOp",EDGE,"E14"),sQuery(id+"F0.wireOp",EDGE,"E15"),sQuery(id+"F0.wireOp",EDGE,"E17.filletArc"),sQuery(id+"F0.wireOp",EDGE,"E18.filletArc"),sQuery(id+"F0.wireOp",EDGE,"E19.filletArc"),sQuery(id+"F0.wireOp",EDGE,"E20.filletArc"),sQuery(id+"F0.wireOp",EDGE,"E25.0"),sQuery(id+"F0.wireOp",EDGE,"E25.1"),sQuery(id+"F0.wireOp",EDGE,"E25.2"),sQuery(id+"F0.wireOp",EDGE,"E25.3"),sQuery(id+"F0.wireOp",EDGE,"E25.4"),sQuery(id+"F0.wireOp",EDGE,"E25.5"),sQuery(id+"F0.wireOp",EDGE,"E25.6"),sQuery(id+"F0.wireOp",EDGE,"E25.7")])],"isStart":false});
            extrude(context, id + "F16", {"entities" : qUnion([Q0, Q1, Q2, Q3]), "endBound" : BoundingType.UP_TO_SURFACE, "endBoundEntityFace" : qUnion([Q4]), "depth" : 25 * mm});
        }
    });
